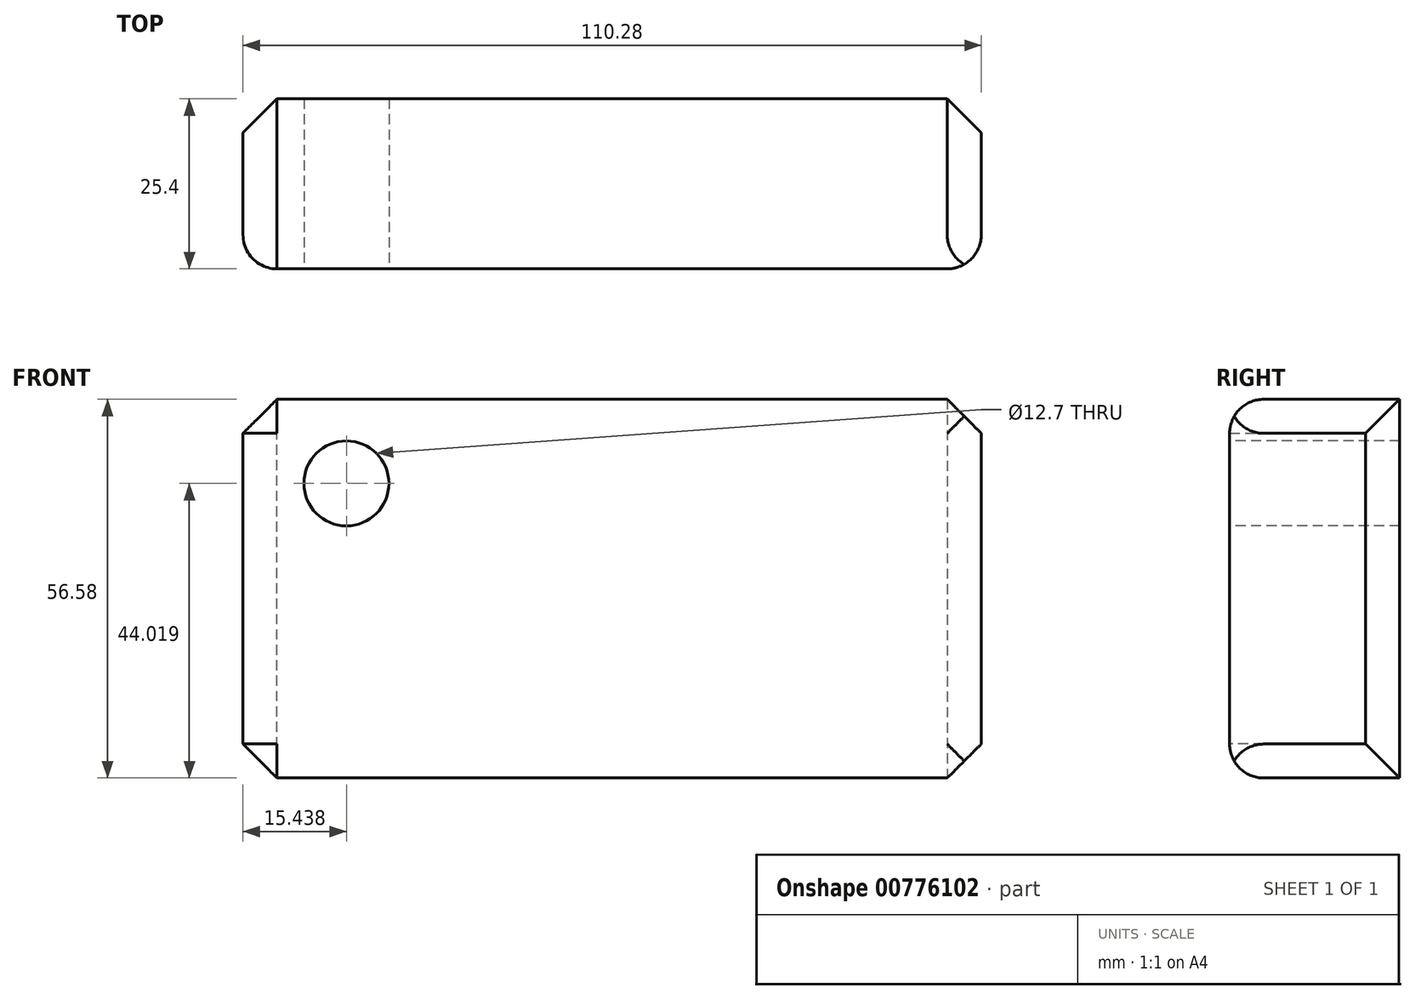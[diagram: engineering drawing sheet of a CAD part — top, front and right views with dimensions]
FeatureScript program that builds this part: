
annotation { "Feature Type Name" : "Feature", "Feature Type Description" : "" }
export const myFeature = defineFeature(function(context is Context, id is Id, definition is map)
    precondition{}
    {
        {
            var Q0;
            Q0=qCreatedBy(makeId("Front.planeOp"),FACE);
            var sketch = newSketch(context, id + "F0", { "sketchPlane" : qUnion([Q0])});
            skLineSegment(sketch, "E0", {"start": v(-58.23, 24.54) * mm, "end": v(52.05, 24.54) * mm});
            skLineSegment(sketch, "E1", {"start": v(52.05, 24.54) * mm, "end": v(52.05, -32.04) * mm});
            skLineSegment(sketch, "E2", {"start": v(52.05, -32.04) * mm, "end": v(-58.23, -32.04) * mm});
            skLineSegment(sketch, "E3", {"start": v(-58.23, -32.04) * mm, "end": v(-58.23, 24.54) * mm});
            skSolve(sketch);
        }
        {
            var Q0;
            Q0=makeQuery(id+"F0.imprint","IMPRINT",FACE,{"disambiguationData":[TD([[makeQuery(id+"F0.imprint","IMPRINT",EDGE,{"derivedFrom":sQuery(id+"F0.wireOp",EDGE,"E0")}),-1.0]])]});
            extrude(context, id + "F1", {"entities" : qUnion([Q0]), "depth" : 25.4 * mm, "offsetDistance" : 25.4 * mm});
        }
        {
            var Q0;
            Q0=makeQuery(id+"F1.opExtrude","CAP_EDGE",EDGE,{"disambiguationData":[OSD([sQuery(id+"F0.wireOp",EDGE,"E3")])],"isStart":false});
            var Q1;
            Q1=makeQuery(id+"F1.opExtrude","CAP_EDGE",EDGE,{"disambiguationData":[OSD([sQuery(id+"F0.wireOp",EDGE,"E0")])],"isStart":false});
            var Q2;
            Q2=makeQuery(id+"F1.opExtrude","CAP_EDGE",EDGE,{"disambiguationData":[OSD([sQuery(id+"F0.wireOp",EDGE,"E1")])],"isStart":false});
            var Q3;
            Q3=makeQuery(id+"F1.opExtrude","CAP_FACE",FACE,{"disambiguationData":[OSD([sQuery(id+"F0.wireOp",EDGE,"E0"),sQuery(id+"F0.wireOp",EDGE,"E1"),sQuery(id+"F0.wireOp",EDGE,"E2"),sQuery(id+"F0.wireOp",EDGE,"E3")])],"isStart":false});
            var Q4;
            Q4=makeQuery(id+"F1.opExtrude","CAP_EDGE",EDGE,{"disambiguationData":[OSD([sQuery(id+"F0.wireOp",EDGE,"E2")])],"isStart":false});
            fillet(context, id + "F2", {"entities" : qUnion([Q0, Q1, Q2, Q3, Q4]), "radius" : 5.08 * mm, "tangentPropagation" : true, "allowEdgeOverflow" : false});
        }
        {
            var Q0;
            Q0=makeQuery(id+"F1.opExtrude","SWEPT_EDGE",EDGE,{"disambiguationData":[OSD([sQuery(id+"F0.wireOp",EDGE,"E0"),sQuery(id+"F0.wireOp",EDGE,"E3")])]});
            var Q1;
            Q1=makeQuery(id+"F1.opExtrude","CAP_EDGE",EDGE,{"disambiguationData":[OSD([sQuery(id+"F0.wireOp",EDGE,"E3")])],"isStart":true});
            var Q2;
            Q2=makeQuery(id+"F1.opExtrude","SWEPT_EDGE",EDGE,{"disambiguationData":[OSD([sQuery(id+"F0.wireOp",EDGE,"E2"),sQuery(id+"F0.wireOp",EDGE,"E3")])]});
            var Q3;
            Q3=makeQuery(id+"F1.opExtrude","SWEPT_EDGE",EDGE,{"disambiguationData":[OSD([sQuery(id+"F0.wireOp",EDGE,"E0"),sQuery(id+"F0.wireOp",EDGE,"E1")])]});
            var Q4;
            Q4=makeQuery(id+"F1.opExtrude","SWEPT_FACE",FACE,{"disambiguationData":[OSD([sQuery(id+"F0.wireOp",EDGE,"E1")])]});
            var Q5;
            Q5=makeQuery(id+"F1.opExtrude","CAP_EDGE",EDGE,{"disambiguationData":[OSD([sQuery(id+"F0.wireOp",EDGE,"E1")])],"isStart":true});
            var Q6;
            Q6=makeQuery(id+"F1.opExtrude","SWEPT_EDGE",EDGE,{"disambiguationData":[OSD([sQuery(id+"F0.wireOp",EDGE,"E1"),sQuery(id+"F0.wireOp",EDGE,"E2")])]});
            chamfer(context, id + "F3", {"entities" : qUnion([Q0, Q1, Q2, Q3, Q4, Q5, Q6]), "width" : 5.08 * mm, "tangentPropagation" : true});
        }
        {
            var Q0;
            Q0=makeQuery(id+"F1.opExtrude","CAP_FACE",FACE,{"disambiguationData":[OSD([sQuery(id+"F0.wireOp",EDGE,"E0"),sQuery(id+"F0.wireOp",EDGE,"E1"),sQuery(id+"F0.wireOp",EDGE,"E2"),sQuery(id+"F0.wireOp",EDGE,"E3")])],"isStart":false});
            var sketch = newSketch(context, id + "F4", { "sketchPlane" : qUnion([Q0])});
            skCircle(sketch, "E4", {"center": v(-42.8, 11.98) * mm, "radius": 6.52 * mm});
            skSolve(sketch);
        }
        {
            var Q0;
            Q0=sQuery(id+"F4.wireOp",VERTEX,"E4.center");
            var Q1;
            Q1=makeQuery(id+"F1.opExtrude","SWEPT_BODY",BODY,{"disambiguationData":[OSD([sQuery(id+"F0.wireOp",EDGE,"E0"),sQuery(id+"F0.wireOp",EDGE,"E1"),sQuery(id+"F0.wireOp",EDGE,"E2"),sQuery(id+"F0.wireOp",EDGE,"E3")])]});
            hole(context, id + "F5", {"style" : HoleStyle.SIMPLE, "endStyle" : HoleEndStyle.THROUGH, "holeDiameter" : 12.7 * mm, "majorDiameter" : 6.35 * mm, "isTappedThrough" : true, "tappedDepth" : 12.7 * mm, "tapClearance" : 3, "locations" : qUnion([Q0]), "scope" : qUnion([Q1])});
        }
    });
